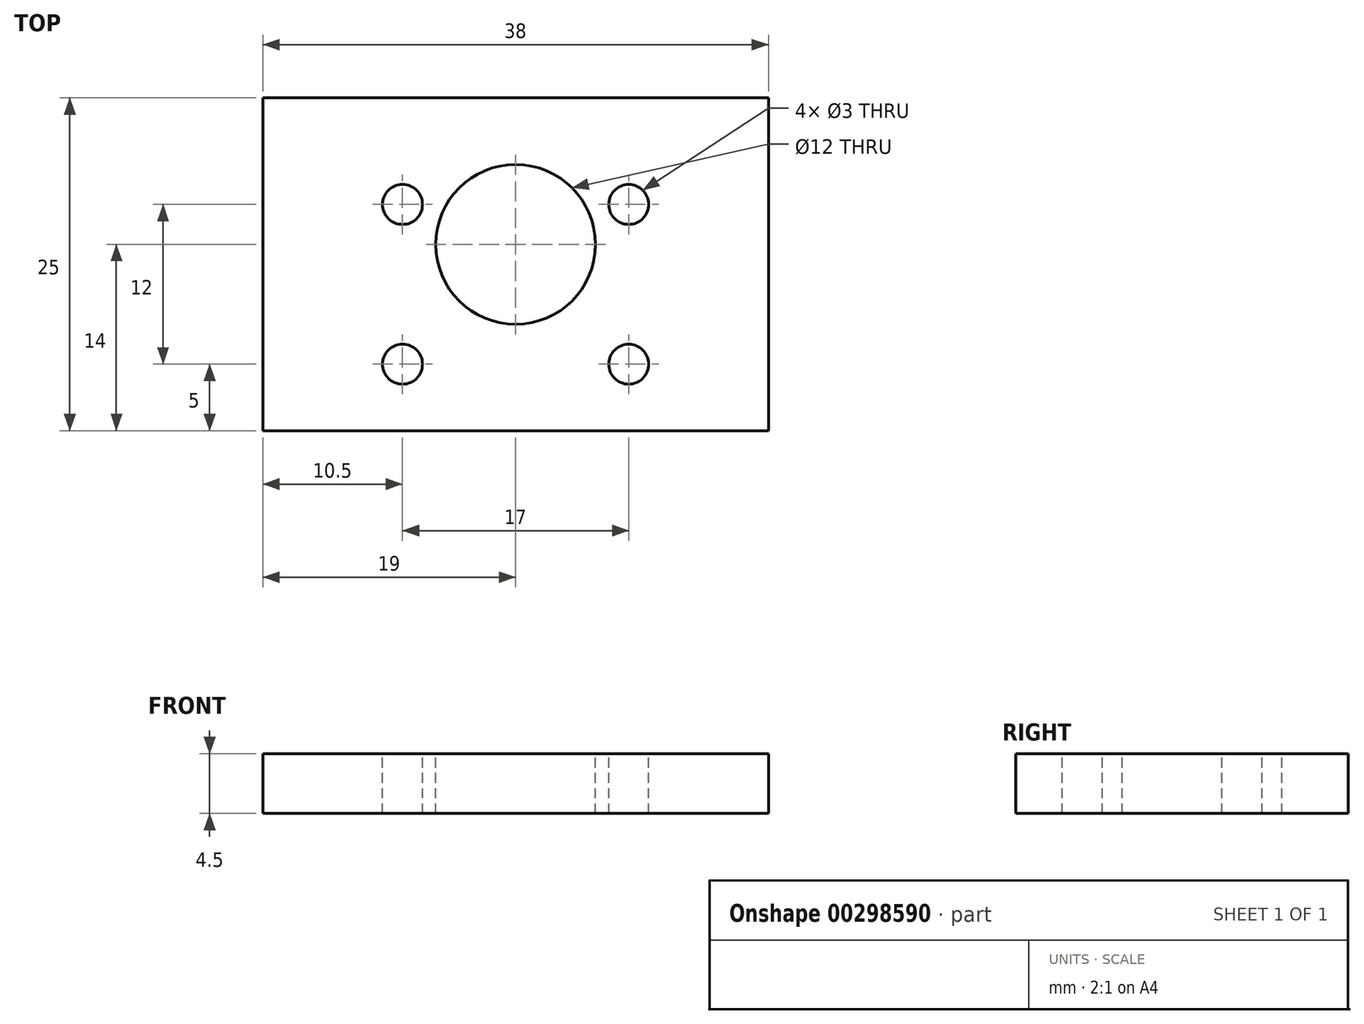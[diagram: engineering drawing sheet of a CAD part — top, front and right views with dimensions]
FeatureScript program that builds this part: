
annotation { "Feature Type Name" : "Feature", "Feature Type Description" : "" }
export const myFeature = defineFeature(function(context is Context, id is Id, definition is map)
    precondition{}
    {
        {
            var Q0;
            Q0=qCreatedBy(makeId("Front.planeOp"),FACE);
            var sketch = newSketch(context, id + "F0", { "sketchPlane" : qUnion([Q0])});
            skLineSegment(sketch, "E0.bottom", {"start": v(-19, 56) * mm, "end": v(19, 56) * mm});
            skLineSegment(sketch, "E0.top", {"start": v(-19, 51.5) * mm, "end": v(19, 51.5) * mm});
            skLineSegment(sketch, "E0.left", {"start": v(-19, 56) * mm, "end": v(-19, 51.5) * mm});
            skLineSegment(sketch, "E0.right", {"start": v(19, 56) * mm, "end": v(19, 51.5) * mm});
            skLineSegment(sketch, "E1.bottom", {"start": v(-15, 51.5) * mm, "end": v(15, 51.5) * mm});
            skSolve(sketch);
        }
        {
            var Q0;
            Q0=qSketchRegion(id+"F0",true);
            extrude(context, id + "F1", {"entities" : qUnion([Q0]), "oppositeDirection" : true, "depth" : 25 * mm});
        }
        {
            var Q0;
            Q0=makeQuery(id+"F1.opExtrude","SWEPT_FACE",FACE,{"disambiguationData":[OSD([sQuery(id+"F0.wireOp",EDGE,"E0.bottom")])]});
            var sketch = newSketch(context, id + "F2", { "sketchPlane" : qUnion([Q0])});
            skCircle(sketch, "E2", {"center": v(0, 14) * mm, "radius": 6 * mm});
            skCircle(sketch, "E3", {"center": v(-8.5, 5) * mm, "radius": 1.5 * mm});
            skCircle(sketch, "E4", {"center": v(8.5, 5) * mm, "radius": 1.5 * mm});
            skCircle(sketch, "E5", {"center": v(-8.5, 17) * mm, "radius": 1.5 * mm});
            skCircle(sketch, "E6", {"center": v(8.5, 17) * mm, "radius": 1.5 * mm});
            skSolve(sketch);
        }
        {
            var Q0;
            Q0=qSketchRegion(id+"F2",true);
            extrude(context, id + "F3", {"entities" : qUnion([Q0]), "operationType" : NewBodyOperationType.REMOVE, "endBound" : BoundingType.UP_TO_NEXT, "oppositeDirection" : true, "depth" : 25 * mm});
        }
    });
